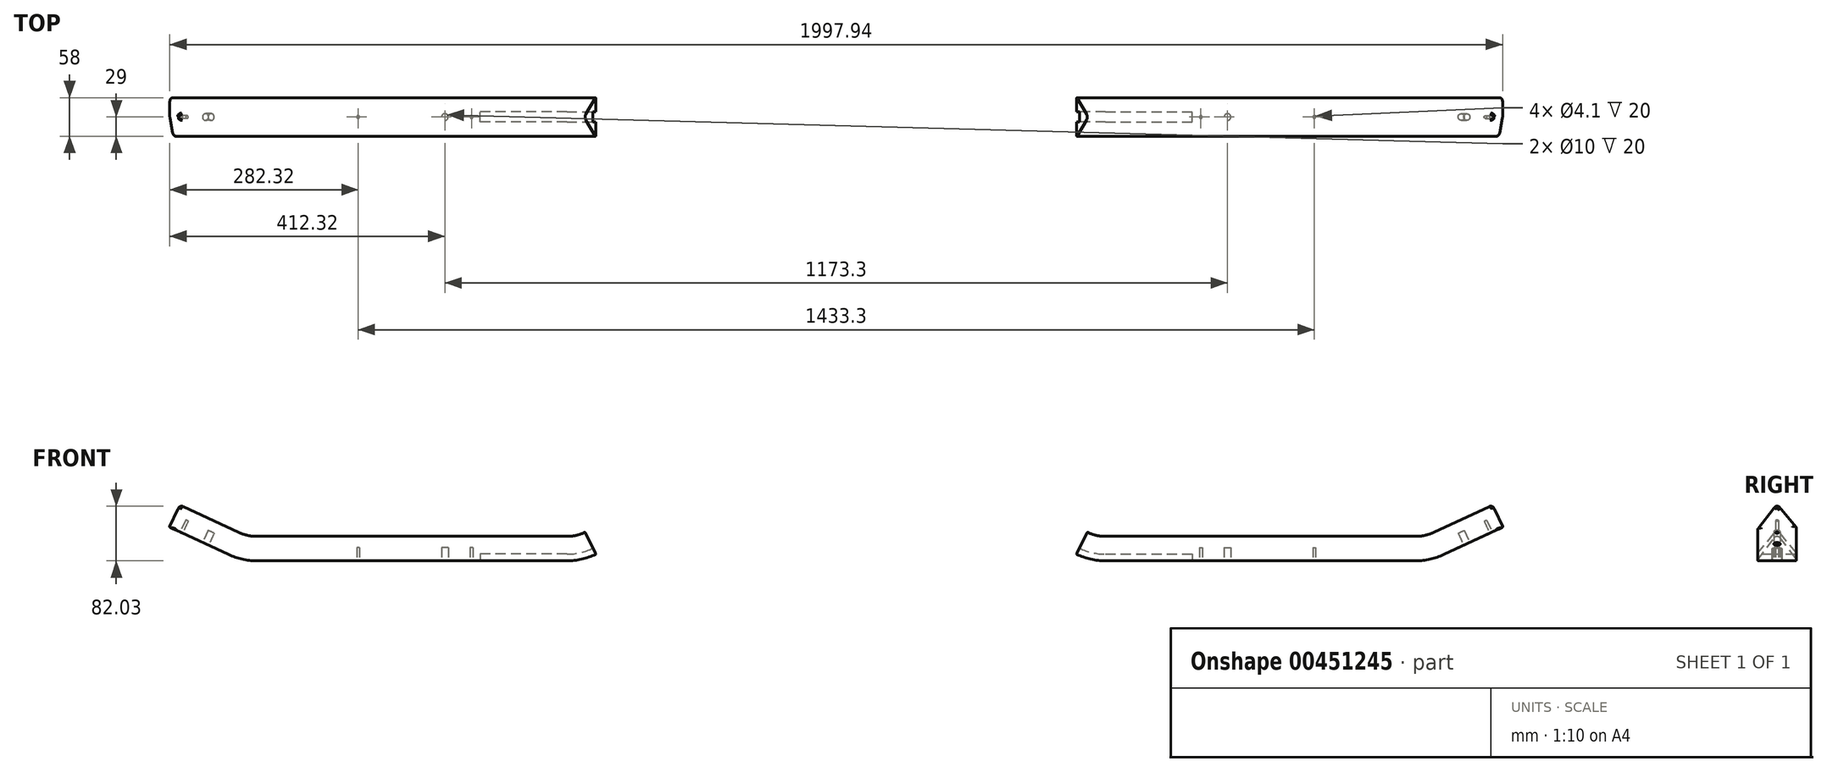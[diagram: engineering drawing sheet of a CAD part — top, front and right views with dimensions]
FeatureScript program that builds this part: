
annotation { "Feature Type Name" : "Feature", "Feature Type Description" : "" }
export const myFeature = defineFeature(function(context is Context, id is Id, definition is map)
    precondition{}
    {
        {
            var Q0;
            Q0=qCreatedBy(makeId("Right.planeOp"),FACE);
            var sketch = newSketch(context, id + "F0", { "sketchPlane" : qUnion([Q0])});
            skLineSegment(sketch, "E0", {"start": v(30, 0) * mm, "end": v(-30, 0) * mm});
            skLineSegment(sketch, "E1", {"start": v(-30, 0) * mm, "end": v(0, 40) * mm});
            skLineSegment(sketch, "E2", {"start": v(0, 40) * mm, "end": v(30, 0) * mm});
            skSolve(sketch);
        }
        {
            var Q0;
            Q0=qCreatedBy(makeId("Front.planeOp"),FACE);
            var sketch = newSketch(context, id + "F1", { "sketchPlane" : qUnion([Q0])});
            skLineSegment(sketch, "E3", {"start": v(0, 0) * mm, "end": v(427.83, 0) * mm});
            skLineSegment(sketch, "E4", {"start": v(470.1, 9.37) * mm, "end": v(558.76, 50.71) * mm});
            skPoint(sketch, "E5.visualSharp", {"position": v(450, 0) * mm});
            skArc(sketch, "E5.filletArc", {"start": v(427.83, 0) * mm, "mid": v(449.47, 2.37) * mm, "end": v(470.1, 9.37) * mm});
            skLineSegment(sketch, "E6", {"start": v(0, 0) * mm, "end": v(-37.3, 0) * mm});
            skPoint(sketch, "E7.visualSharp", {"position": v(-83.93, 0) * mm});
            skArc(sketch, "E7.filletArc", {"start": v(-80.52, 9.82) * mm, "mid": v(-59.46, 2.49) * mm, "end": v(-37.3, 0) * mm});
            skSolve(sketch);
        }
        {
            var Q0;
            Q0 = qSketchRegion(id + "F0", true);
            var Q1;
            Q1=sQuery(id+"F1.wireOp",EDGE,"E6");
            var Q2;
            Q2=sQuery(id+"F1.wireOp",EDGE,"E7.filletArc");
            var Q3;
            Q3=sQuery(id+"F1.wireOp",EDGE,"4lItoZta-QgLP-WyET-9Vek-mWAvu2dLh5lC");
            var Q4;
            Q4=sQuery(id+"F1.wireOp",EDGE,"E3");
            var Q5;
            Q5=sQuery(id+"F1.wireOp",EDGE,"E5.filletArc");
            var Q6;
            Q6=sQuery(id+"F1.wireOp",EDGE,"E4");
            sweep(context, id + "F2", {"profiles" : qUnion([Q0]), "path" : qUnion([Q1, Q2, Q3, Q4, Q5, Q6])});
        }
        {
            var Q0;
            Q0=makeQuery(id+"F2.opSweep","SWEPT_EDGE",EDGE,{"disambiguationData":[OSD([sQuery(id+"F0.wireOp",EDGE,"E1"),sQuery(id+"F0.wireOp",EDGE,"E2"),sQuery(id+"F1.wireOp",EDGE,"E6")])]});
            fillet(context, id + "F3", {"entities" : qUnion([Q0]), "tangentPropagation" : true, "radius" : 5 * mm, "defaultsChanged" : true, "vertexSettings" : [], "allowEdgeOverflow" : false});
        }
        {
            var Q0;
            Q0=makeQuery(id+"F2.opSweep","SWEPT_FACE",FACE,{"disambiguationData":[OSD([sQuery(id+"F0.wireOp",EDGE,"E0"),sQuery(id+"F1.wireOp",EDGE,"E4")])]});
            var sketch = newSketch(context, id + "F4", { "sketchPlane" : qUnion([Q0])});
            skCircle(sketch, "E8", {"center": v(467.84, 0) * mm, "radius": 5 * mm});
            skPoint(sketch, "E8.centerSnap0", {"position": v(527.84, 0) * mm});
            skCircle(sketch, "E9", {"center": v(507.84, 0) * mm, "radius": 2.05 * mm});
            skSolve(sketch);
        }
        {
            var Q0;
            Q0 = qSketchRegion(id + "F4", true);
            extrude(context, id + "F5", {"entities" : qUnion([Q0]), "operationType" : NewBodyOperationType.REMOVE, "oppositeDirection" : true, "depth" : 20 * mm, "offsetDistance" : 25 * mm});
        }
        {
            var Q0;
            Q0=makeQuery(id+"F2.opSweep","SWEPT_FACE",FACE,{"disambiguationData":[OSD([sQuery(id+"F0.wireOp",EDGE,"E0"),sQuery(id+"F1.wireOp",EDGE,"E6")])]});
            var sketch = newSketch(context, id + "F6", { "sketchPlane" : qUnion([Q0])});
            skCircle(sketch, "E10", {"center": v(105.65, 0) * mm, "radius": 2.05 * mm});
            skCircle(sketch, "E11", {"center": v(145.65, 0) * mm, "radius": 5 * mm});
            skCircle(sketch, "E12", {"center": v(275.65, 0) * mm, "radius": 2.05 * mm});
            skSolve(sketch);
        }
        {
            var Q0;
            Q0 = qSketchRegion(id + "F6", true);
            extrude(context, id + "F7", {"entities" : qUnion([Q0]), "operationType" : NewBodyOperationType.REMOVE, "oppositeDirection" : true, "depth" : 20 * mm, "offsetDistance" : 25 * mm});
        }
        {
            var Q0;
            Q0=makeQuery(id+"F2.opSweep","SWEPT_FACE",FACE,{"disambiguationData":[OSD([sQuery(id+"F0.wireOp",EDGE,"E0"),sQuery(id+"F1.wireOp",EDGE,"E6")])]});
            var sketch = newSketch(context, id + "F8", { "sketchPlane" : qUnion([Q0])});
            skLineSegment(sketch, "E13.bottom", {"start": v(-37.3, 7.5) * mm, "end": v(92.7, 7.5) * mm});
            skLineSegment(sketch, "E13.top", {"start": v(-37.3, -7.5) * mm, "end": v(92.7, -7.5) * mm});
            skLineSegment(sketch, "E13.left", {"start": v(-37.3, 7.5) * mm, "end": v(-37.3, -7.5) * mm});
            skLineSegment(sketch, "E13.right", {"start": v(92.7, 7.5) * mm, "end": v(92.7, -7.5) * mm});
            skPoint(sketch, "E13.middle", {"position": v(27.7, 0) * mm});
            skSolve(sketch);
        }
        {
            var Q0;
            Q0 = qSketchRegion(id + "F8", true);
            extrude(context, id + "F9", {"entities" : qUnion([Q0]), "operationType" : NewBodyOperationType.REMOVE, "oppositeDirection" : true, "depth" : 10 * mm, "offsetDistance" : 25 * mm});
        }
        {
            var Q0;
            Q0=makeQuery(id+"F9.boolean.opBoolean","COPY",FACE,{"derivedFrom":makeQuery(id+"F9.opExtrude","SWEPT_FACE",FACE,{"disambiguationData":[OSD([sQuery(id+"F8.wireOp",EDGE,"E13.left")])]})});
            var Q1;
            Q1=makeQuery(id+"F2.opSweep","SWEPT_EDGE",EDGE,{"disambiguationData":[OSD([sQuery(id+"F0.wireOp",EDGE,"E0"),sQuery(id+"F0.wireOp",EDGE,"E2"),sQuery(id+"F1.wireOp",EDGE,"E7.filletArc")])]});
            sweep(context, id + "F10", {"operationType" : NewBodyOperationType.REMOVE, "profiles" : qUnion([Q0]), "path" : qUnion([Q1])});
        }
        {
            var Q0;
            Q0=makeQuery(id+"F2.opSweep","SWEPT_FACE",FACE,{"disambiguationData":[OSD([sQuery(id+"F0.wireOp",EDGE,"E0"),sQuery(id+"F1.wireOp",EDGE,"E4")])]});
            var sketch = newSketch(context, id + "F11", { "sketchPlane" : qUnion([Q0])});
            skLineSegment(sketch, "E14", {"start": v(527.84, -30) * mm, "end": v(527.34, -30) * mm});
            skLineSegment(sketch, "E15", {"start": v(527.34, -30) * mm, "end": v(527.34, -2.01) * mm});
            skLineSegment(sketch, "E16", {"start": v(526.94, 1.97) * mm, "end": v(521.23, 30) * mm});
            skLineSegment(sketch, "E17", {"start": v(521.23, 30) * mm, "end": v(527.84, 30) * mm});
            skLineSegment(sketch, "E18", {"start": v(527.84, 30) * mm, "end": v(527.84, -30) * mm});
            skPoint(sketch, "E19", {"position": v(527.84, 0) * mm});
            skPoint(sketch, "E20.visualSharp", {"position": v(527.34, 0) * mm});
            skArc(sketch, "E20.filletArc", {"start": v(527.34, -2.01) * mm, "mid": v(527.24, -0.01) * mm, "end": v(526.94, 1.97) * mm});
            skSolve(sketch);
        }
        {
            var Q0;
            Q0 = qSketchRegion(id + "F11", true);
            extrude(context, id + "F12", {"entities" : qUnion([Q0]), "operationType" : NewBodyOperationType.REMOVE, "endBound" : BoundingType.THROUGH_ALL, "oppositeDirection" : true, "depth" : 25 * mm, "offsetDistance" : 25 * mm});
        }
        {
            var Q0;
            Q0=makeQuery(id+"F12.boolean.opBoolean","INTERSECT",EDGE,{"derivedFrom":[makeQuery(id+"F2.opSweep","SWEPT_FACE",FACE,{"disambiguationData":[OSD([sQuery(id+"F0.wireOp",EDGE,"E2"),sQuery(id+"F1.wireOp",EDGE,"E4")])]}),makeQuery(id+"F12.opExtrude","SWEPT_FACE",FACE,{"disambiguationData":[OSD([sQuery(id+"F11.wireOp",EDGE,"E15")])]})]});
            fillet(context, id + "F13", {"entities" : qUnion([Q0]), "tangentPropagation" : true, "radius" : 5 * mm, "defaultsChanged" : false, "vertexSettings" : [], "allowEdgeOverflow" : false});
        }
        {
            var Q0;
            Q0=makeQuery(id+"F2.opSweep","SWEPT_EDGE",EDGE,{"disambiguationData":[OSD([sQuery(id+"F0.wireOp",EDGE,"E0"),sQuery(id+"F0.wireOp",EDGE,"E2"),sQuery(id+"F1.wireOp",EDGE,"E4")])]});
            var Q1;
            Q1=makeQuery(id+"F2.opSweep","SWEPT_EDGE",EDGE,{"disambiguationData":[OSD([sQuery(id+"F0.wireOp",EDGE,"E0"),sQuery(id+"F0.wireOp",EDGE,"E1"),sQuery(id+"F1.wireOp",EDGE,"E6")])]});
            fillet(context, id + "F14", {"entities" : qUnion([Q0, Q1]), "tangentPropagation" : true, "radius" : 1 * mm, "defaultsChanged" : false, "vertexSettings" : [], "allowEdgeOverflow" : false});
        }
        {
            var Q0;
            Q0=qCreatedBy(makeId("Right.planeOp"),FACE);
            cPlane(context, id + "F15", {"entities" : qUnion([Q0]), "cplaneType" : CPlaneType.OFFSET, "offset" : 441 * mm, "oppositeDirection" : true, "width" : 150 * mm, "height" : 150 * mm});
        }
        {
            var Q0;
            Q0=makeQuery(id+"F2.opSweep","SWEPT_BODY",BODY,{"disambiguationData":[OSD([sQuery(id+"F0.wireOp",EDGE,"E0"),sQuery(id+"F0.wireOp",EDGE,"E1"),sQuery(id+"F0.wireOp",EDGE,"E2"),sQuery(id+"F1.wireOp",EDGE,"E4")])]});
            var Q1;
            Q1=qCreatedBy(id+"F15.planeOp",FACE);
            mirror(context, id + "F16", {"entities" : qUnion([Q0]), "mirrorPlane" : qUnion([Q1])});
        }
    });
